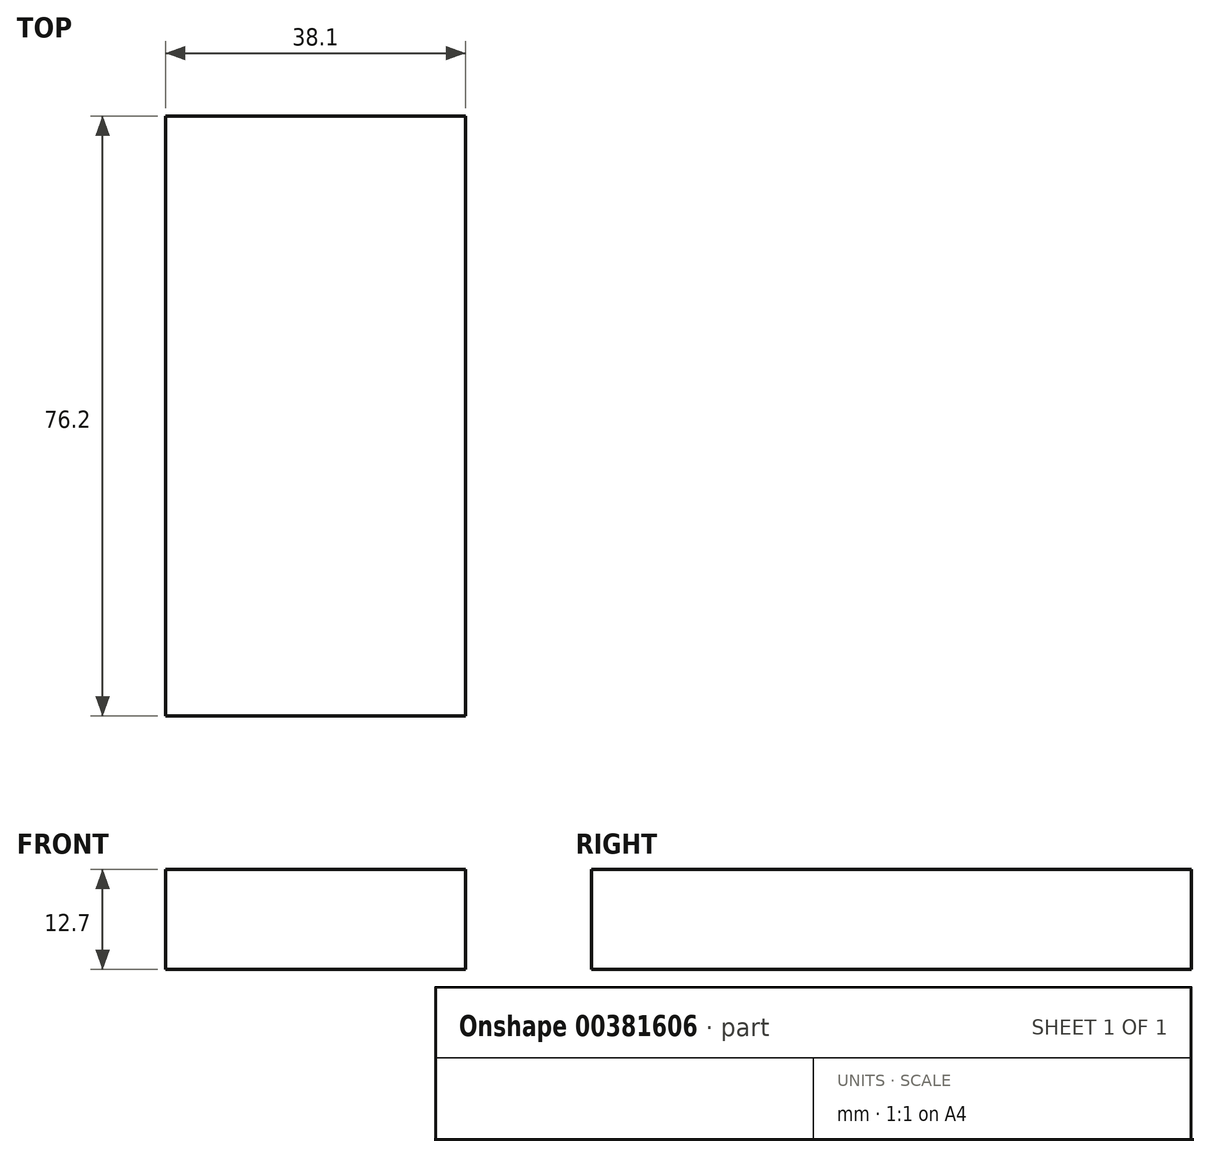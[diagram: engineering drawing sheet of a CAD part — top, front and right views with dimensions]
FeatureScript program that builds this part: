
annotation { "Feature Type Name" : "Feature", "Feature Type Description" : "" }
export const myFeature = defineFeature(function(context is Context, id is Id, definition is map)
    precondition{}
    {
        {
            var Q0;
            Q0=qCreatedBy(makeId("Front.planeOp"),FACE);
            var sketch = newSketch(context, id + "F0", { "sketchPlane" : qUnion([Q0])});
            skLineSegment(sketch, "E0.bottom", {"start": v(19.05, -6.35) * mm, "end": v(-19.05, -6.35) * mm});
            skLineSegment(sketch, "E0.top", {"start": v(19.05, 6.35) * mm, "end": v(-19.05, 6.35) * mm});
            skLineSegment(sketch, "E0.left", {"start": v(19.05, -6.35) * mm, "end": v(19.05, 6.35) * mm});
            skLineSegment(sketch, "E0.right", {"start": v(-19.05, -6.35) * mm, "end": v(-19.05, 6.35) * mm});
            skPoint(sketch, "E0.middle", {"position": v(0, 0) * mm});
            skSolve(sketch);
        }
        {
            var Q0;
            Q0=qCreatedBy(makeId("Front.planeOp"),FACE);
            cPlane(context, id + "F1", {"entities" : qUnion([Q0]), "cplaneType" : CPlaneType.OFFSET, "offset" : 76.2 * mm, "width" : 152.4 * mm, "height" : 152.4 * mm});
        }
        {
            var Q0;
            Q0=makeQuery(id+"F0.imprint","IMPRINT",FACE,{"disambiguationData":[TD([[makeQuery(id+"F0.imprint","IMPRINT",EDGE,{"derivedFrom":sQuery(id+"F0.wireOp",EDGE,"E0.bottom")}),-1.0]])]});
            extrude(context, id + "F2", {"entities" : qUnion([Q0]), "endBound" : BoundingType.SYMMETRIC, "depth" : 76.2 * mm});
        }
        {
            var Q0;
            Q0=qCreatedBy(makeId("Right.planeOp"),FACE);
            var sketch = newSketch(context, id + "F3", { "sketchPlane" : qUnion([Q0])});
            skLineSegment(sketch, "E1", {"start": v(-38.12, 12) * mm, "end": v(-76, -17.18) * mm});
            skLineSegment(sketch, "E2", {"start": v(-76, -17.18) * mm, "end": v(-76, -42.12) * mm});
            skLineSegment(sketch, "E3", {"start": v(-76, -42.12) * mm, "end": v(-37.89, -12.7) * mm});
            skSolve(sketch);
        }
        {
            var Q0;
            Q0=sQuery(id+"F3.wireOp",EDGE,"E3");
            extrude(context, id + "F4", {"bodyType" : ToolBodyType.SURFACE, "surfaceEntities" : qUnion([Q0]), "endBound" : BoundingType.SYMMETRIC, "depth" : 38.1 * mm});
        }
    });
